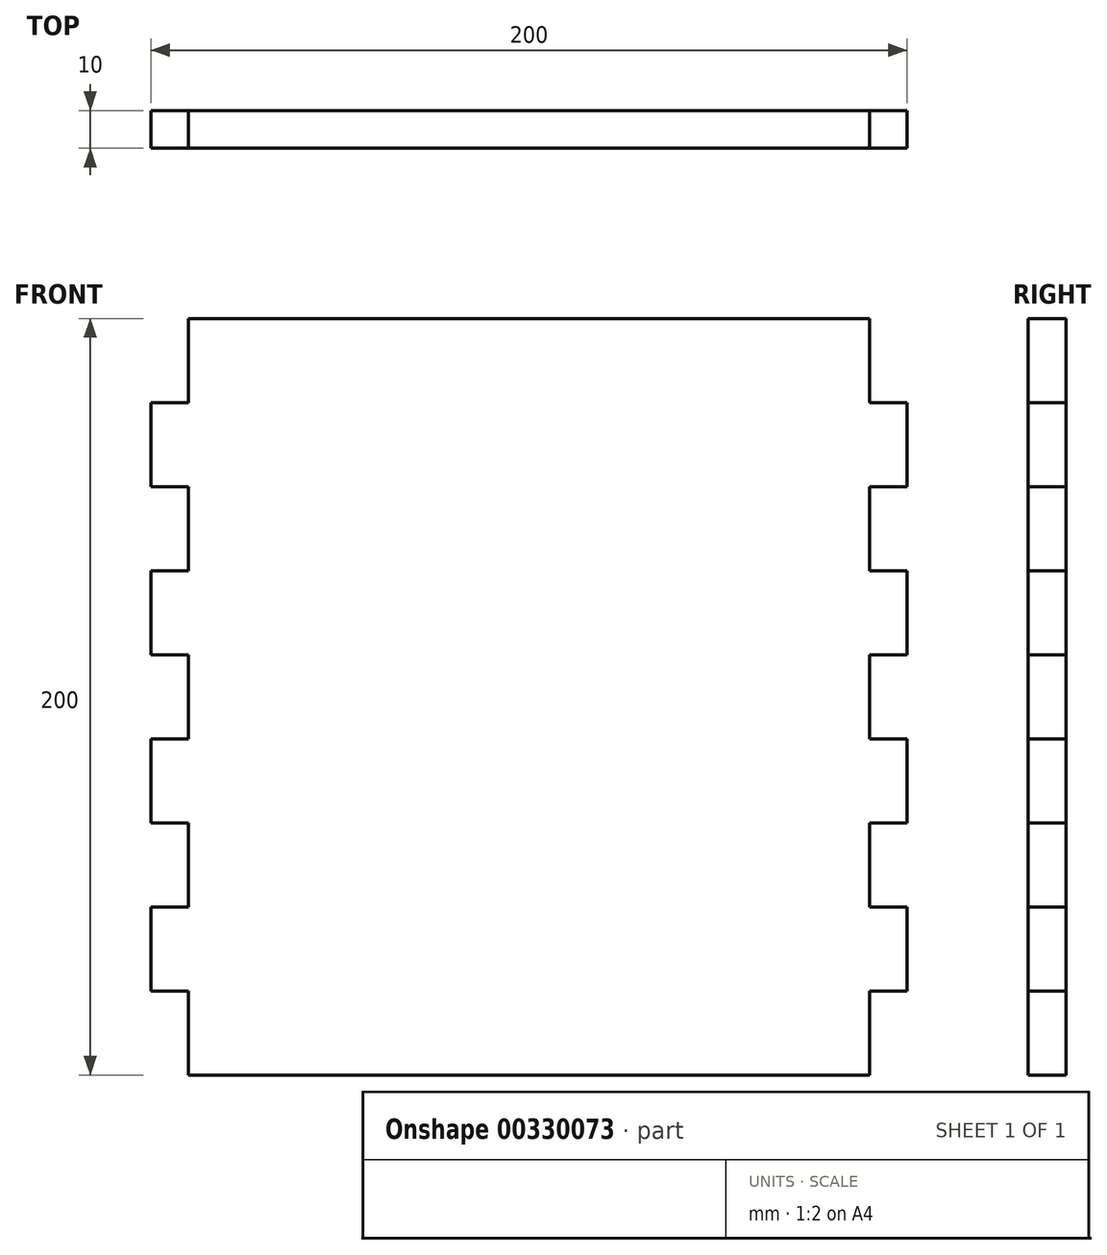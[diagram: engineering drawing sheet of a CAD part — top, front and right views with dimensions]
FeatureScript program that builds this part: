
annotation { "Feature Type Name" : "Feature", "Feature Type Description" : "" }
export const myFeature = defineFeature(function(context is Context, id is Id, definition is map)
    precondition{}
    {
        {
            var Q0;
            Q0=qCreatedBy(makeId("Front.planeOp"),FACE);
            var sketch = newSketch(context, id + "F0", { "sketchPlane" : qUnion([Q0])});
            skLineSegment(sketch, "E0.bottom", {"start": v(-214.3, -79.35) * mm, "end": v(-34.3, -79.35) * mm});
            skLineSegment(sketch, "E0.right", {"start": v(-24.3, -101.57) * mm, "end": v(-24.3, -123.8) * mm});
            skLineSegment(sketch, "E1", {"start": v(-214.3, -79.35) * mm, "end": v(-214.3, -101.57) * mm});
            skLineSegment(sketch, "E2", {"start": v(-34.3, -79.35) * mm, "end": v(-34.3, -101.57) * mm});
            skLineSegment(sketch, "E3", {"start": v(-224.3, -101.57) * mm, "end": v(-214.3, -101.57) * mm});
            skLineSegment(sketch, "E4", {"start": v(-224.3, -123.8) * mm, "end": v(-214.3, -123.8) * mm});
            skLineSegment(sketch, "E5", {"start": v(-224.3, -146.02) * mm, "end": v(-214.3, -146.02) * mm});
            skLineSegment(sketch, "E6", {"start": v(-224.3, -190.46) * mm, "end": v(-214.3, -190.46) * mm});
            skLineSegment(sketch, "E7", {"start": v(-224.3, -168.24) * mm, "end": v(-214.3, -168.24) * mm});
            skLineSegment(sketch, "E8", {"start": v(-224.3, -234.9) * mm, "end": v(-214.3, -234.9) * mm});
            skLineSegment(sketch, "E9", {"start": v(-224.3, -257.13) * mm, "end": v(-214.3, -257.13) * mm});
            skLineSegment(sketch, "E10", {"start": v(-224.3, -212.68) * mm, "end": v(-214.3, -212.68) * mm});
            skLineSegment(sketch, "E11", {"start": v(-214.3, -279.35) * mm, "end": v(-34.3, -279.35) * mm});
            skLineSegment(sketch, "E12", {"start": v(-34.3, -101.57) * mm, "end": v(-24.3, -101.57) * mm});
            skLineSegment(sketch, "E13", {"start": v(-34.3, -123.8) * mm, "end": v(-24.3, -123.8) * mm});
            skLineSegment(sketch, "E14", {"start": v(-34.3, -146.02) * mm, "end": v(-24.3, -146.02) * mm});
            skLineSegment(sketch, "E15", {"start": v(-34.3, -190.46) * mm, "end": v(-24.3, -190.46) * mm});
            skLineSegment(sketch, "E16", {"start": v(-34.3, -168.24) * mm, "end": v(-24.3, -168.24) * mm});
            skLineSegment(sketch, "E17", {"start": v(-34.3, -234.9) * mm, "end": v(-24.3, -234.9) * mm});
            skLineSegment(sketch, "E18", {"start": v(-34.3, -257.13) * mm, "end": v(-24.3, -257.13) * mm});
            skLineSegment(sketch, "E19", {"start": v(-34.3, -212.68) * mm, "end": v(-24.3, -212.68) * mm});
            skLineSegment(sketch, "E20", {"start": v(-224.3, -101.57) * mm, "end": v(-224.3, -123.8) * mm});
            skLineSegment(sketch, "E21.trimOffspring", {"start": v(-24.3, -146.02) * mm, "end": v(-24.3, -168.24) * mm});
            skLineSegment(sketch, "E22.trimOffspring", {"start": v(-24.3, -190.46) * mm, "end": v(-24.3, -212.68) * mm});
            skLineSegment(sketch, "E23.trimOffspring", {"start": v(-24.3, -234.9) * mm, "end": v(-24.3, -257.13) * mm});
            skLineSegment(sketch, "E24.trimOffspring", {"start": v(-224.3, -146.02) * mm, "end": v(-224.3, -168.24) * mm});
            skLineSegment(sketch, "E25.trimOffspring", {"start": v(-224.3, -190.46) * mm, "end": v(-224.3, -212.68) * mm});
            skLineSegment(sketch, "E26.trimOffspring", {"start": v(-224.3, -234.9) * mm, "end": v(-224.3, -257.13) * mm});
            skLineSegment(sketch, "E27.trimOffspring", {"start": v(-214.3, -123.8) * mm, "end": v(-214.3, -146.02) * mm});
            skLineSegment(sketch, "E28.trimOffspring", {"start": v(-214.3, -168.24) * mm, "end": v(-214.3, -190.46) * mm});
            skLineSegment(sketch, "E29.trimOffspring", {"start": v(-214.3, -212.68) * mm, "end": v(-214.3, -234.9) * mm});
            skLineSegment(sketch, "E30.trimOffspring", {"start": v(-214.3, -257.13) * mm, "end": v(-214.3, -279.35) * mm});
            skLineSegment(sketch, "E31.trimOffspring", {"start": v(-34.3, -257.13) * mm, "end": v(-34.3, -279.35) * mm});
            skLineSegment(sketch, "E32.trimOffspring", {"start": v(-34.3, -212.68) * mm, "end": v(-34.3, -234.9) * mm});
            skLineSegment(sketch, "E33.trimOffspring", {"start": v(-34.3, -168.24) * mm, "end": v(-34.3, -190.46) * mm});
            skLineSegment(sketch, "E34.trimOffspring", {"start": v(-34.3, -123.8) * mm, "end": v(-34.3, -146.02) * mm});
            skSolve(sketch);
        }
        {
            var Q0;
            Q0 = qSketchRegion(id + "F0", true);
            extrude(context, id + "F1", {"entities" : qUnion([Q0]), "depth" : 10 * mm, "offsetDistance" : 25 * mm});
        }
    });
